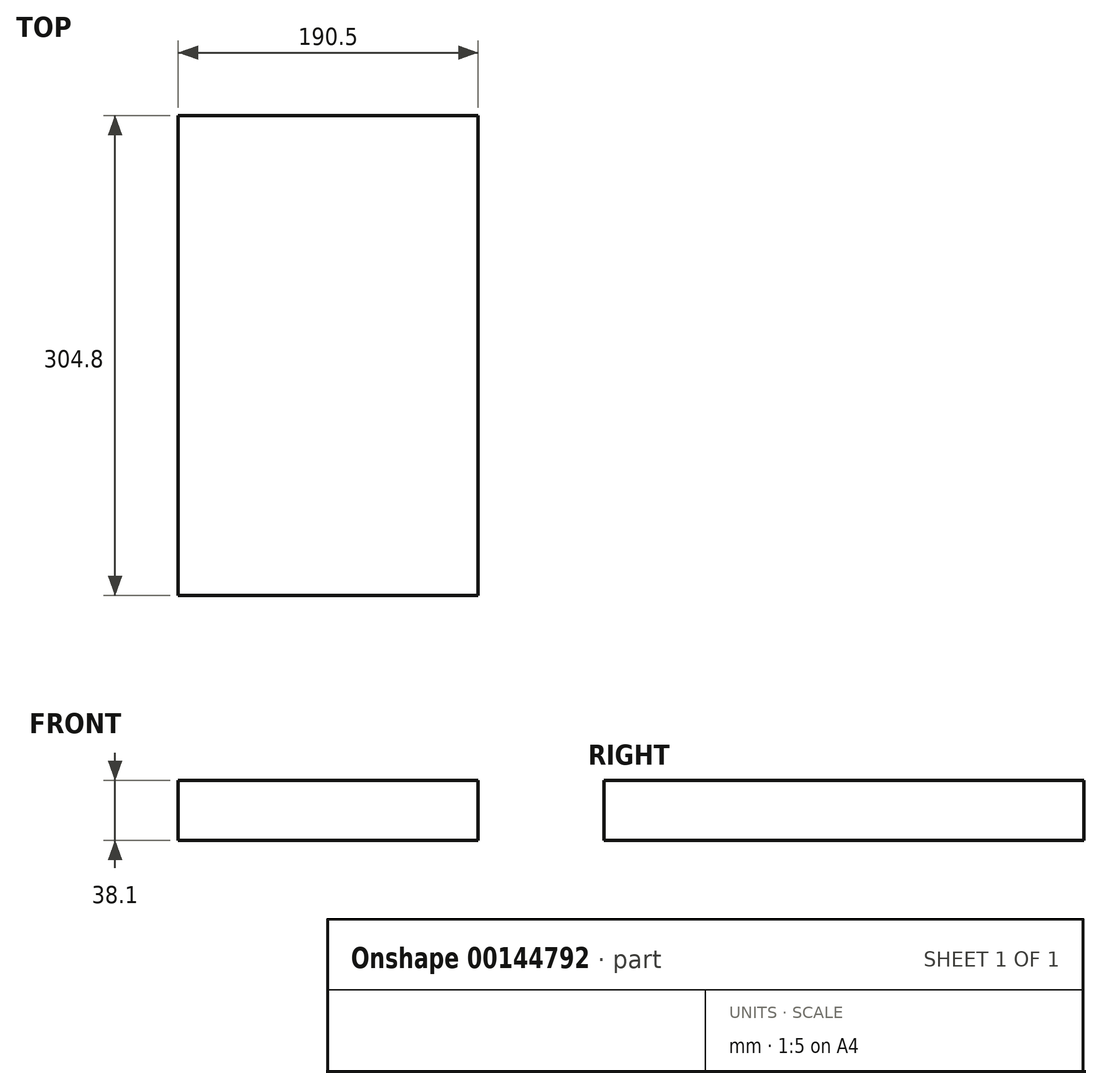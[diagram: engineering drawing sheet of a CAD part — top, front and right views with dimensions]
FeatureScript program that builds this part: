
annotation { "Feature Type Name" : "Feature", "Feature Type Description" : "" }
export const myFeature = defineFeature(function(context is Context, id is Id, definition is map)
    precondition{}
    {
        {
            var Q0;
            Q0=qCreatedBy(makeId("Front.planeOp"),FACE);
            var sketch = newSketch(context, id + "F0", { "sketchPlane" : qUnion([Q0])});
            skLineSegment(sketch, "E0.bottom", {"start": v(0, 0) * mm, "end": v(190.5, 0) * mm});
            skLineSegment(sketch, "E0.top", {"start": v(0, 38.1) * mm, "end": v(190.5, 38.1) * mm});
            skLineSegment(sketch, "E0.left", {"start": v(0, 0) * mm, "end": v(0, 38.1) * mm});
            skLineSegment(sketch, "E0.right", {"start": v(190.5, 0) * mm, "end": v(190.5, 38.1) * mm});
            skSolve(sketch);
        }
        {
            var Q0;
            Q0=makeQuery(id+"F0.imprint","IMPRINT",FACE,{"disambiguationData":[TD([[makeQuery(id+"F0.imprint","IMPRINT",EDGE,{"derivedFrom":sQuery(id+"F0.wireOp",EDGE,"E0.bottom")}),1.0]])]});
            extrude(context, id + "F1", {"entities" : qUnion([Q0]), "depth" : 304.8 * mm});
        }
    });
